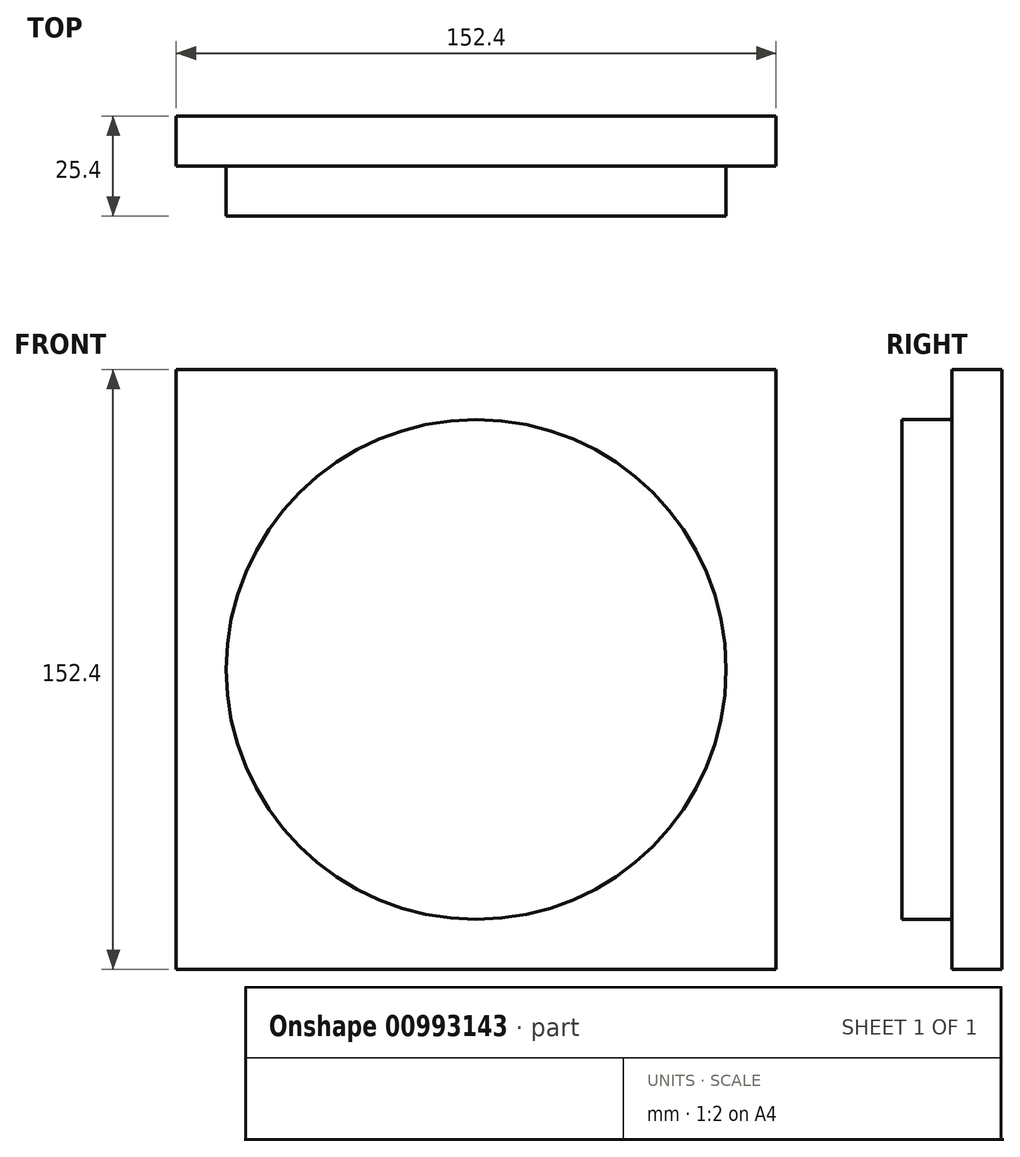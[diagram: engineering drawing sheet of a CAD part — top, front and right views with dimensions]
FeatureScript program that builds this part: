
annotation { "Feature Type Name" : "Feature", "Feature Type Description" : "" }
export const myFeature = defineFeature(function(context is Context, id is Id, definition is map)
    precondition{}
    {
        {
            var Q0;
            Q0=qCreatedBy(makeId("Front.planeOp"),FACE);
            var sketch = newSketch(context, id + "F0", { "sketchPlane" : qUnion([Q0])});
            skLineSegment(sketch, "E0.bottom", {"start": v(-91.15, 79.7) * mm, "end": v(61.25, 79.7) * mm});
            skLineSegment(sketch, "E0.top", {"start": v(-91.15, -72.7) * mm, "end": v(61.25, -72.7) * mm});
            skLineSegment(sketch, "E0.left", {"start": v(-91.15, 79.7) * mm, "end": v(-91.15, -72.7) * mm});
            skLineSegment(sketch, "E0.right", {"start": v(61.25, 79.7) * mm, "end": v(61.25, -72.7) * mm});
            skCircle(sketch, "E1", {"center": v(-14.95, 3.5) * mm, "radius": 63.5 * mm});
            skPoint(sketch, "E1.centerSnap0", {"position": v(-14.95, 79.7) * mm});
            skSolve(sketch);
        }
        {
            var Q0;
            Q0=makeQuery(id+"F0.imprint","IMPRINT",FACE,{"disambiguationData":[TD([[makeQuery(id+"F0.imprint","IMPRINT",EDGE,{"derivedFrom":sQuery(id+"F0.wireOp",EDGE,"E0.bottom")}),-1.0]])]});
            extrude(context, id + "F1", {"entities" : qUnion([Q0]), "depth" : 12.7 * mm, "offsetDistance" : 25.4 * mm});
        }
        {
            var Q0;
            Q0=makeQuery(id+"F0.imprint","IMPRINT",FACE,{"disambiguationData":[TD([[makeQuery(id+"F0.imprint","IMPRINT",EDGE,{"derivedFrom":sQuery(id+"F0.wireOp",EDGE,"E1")}),1.0]])]});
            extrude(context, id + "F2", {"entities" : qUnion([Q0]), "operationType" : NewBodyOperationType.ADD, "depth" : 25.4 * mm, "offsetDistance" : 25.4 * mm});
        }
    });
